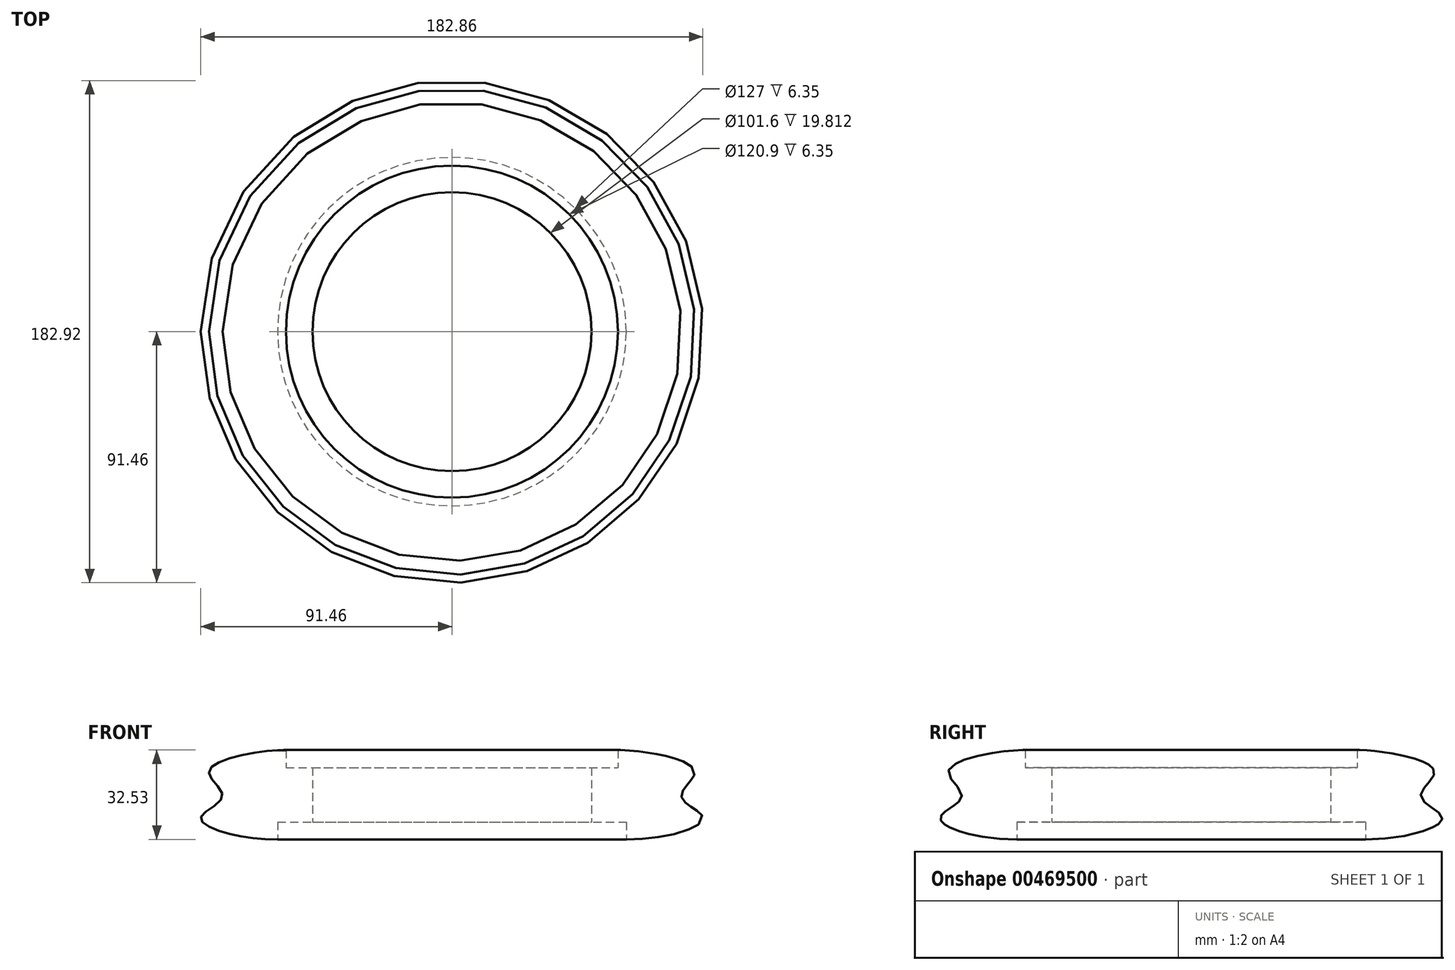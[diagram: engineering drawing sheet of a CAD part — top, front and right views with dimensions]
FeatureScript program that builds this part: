
annotation { "Feature Type Name" : "Feature", "Feature Type Description" : "" }
export const myFeature = defineFeature(function(context is Context, id is Id, definition is map)
    precondition{}
    {
        {
            var Q0;
            Q0=qCreatedBy(makeId("Front.planeOp"),FACE);
            var sketch = newSketch(context, id + "F0", { "sketchPlane" : qUnion([Q0])});
            skLineSegment(sketch, "E0", {"start": v(0, 0) * mm, "end": v(-63.5, 0) * mm, "construction": true});
            skLineSegment(sketch, "E1", {"start": v(0, 0) * mm, "end": v(0, 31.75) * mm, "construction": true});
            skLineSegment(sketch, "E2", {"start": v(-63.5, 0) * mm, "end": v(-63.5, 31.75) * mm, "construction": true});
            skLineSegment(sketch, "E3", {"start": v(-63.5, 31.75) * mm, "end": v(-69.85, 31.75) * mm, "construction": true});
            skLineSegment(sketch, "E4", {"start": v(-69.85, 31.75) * mm, "end": v(-69.85, 25.4) * mm, "construction": true});
            skLineSegment(sketch, "E5", {"start": v(-69.85, 25.4) * mm, "end": v(-69.85, 6.35) * mm, "construction": true});
            skLineSegment(sketch, "E6", {"start": v(-69.85, 6.35) * mm, "end": v(-69.85, 0) * mm, "construction": true});
            skSolve(sketch);
        }
        {
            var Q0;
            Q0=qCreatedBy(makeId("Front.planeOp"),FACE);
            var sketch = newSketch(context, id + "F1", { "sketchPlane" : qUnion([Q0])});
            skLineSegment(sketch, "E7", {"start": v(-60.45, 26.16) * mm, "end": v(-50.8, 26.16) * mm});
            skLineSegment(sketch, "E8", {"start": v(-60.45, 26.16) * mm, "end": v(-60.45, 32.51) * mm});
            skLineSegment(sketch, "E9", {"start": v(-63.5, 0) * mm, "end": v(-63.5, 6.35) * mm});
            skLineSegment(sketch, "E10", {"start": v(-63.5, 6.35) * mm, "end": v(-50.8, 6.35) * mm});
            skLineSegment(sketch, "E11", {"start": v(-50.8, 6.35) * mm, "end": v(-50.8, 26.16) * mm});
            skFitSpline(sketch, "E12", {"points": [v(-60.45, 32.51) * mm, v(-79.69, 29.9) * mm, v(-88.48, 23.87) * mm, v(-83.57, 15.59) * mm, v(-91.34, 8.31) * mm, v(-84.55, 3) * mm, v(-63.5, 0) * mm], "startDerivative": vector(-54.07, 2.17) * mm, "endDerivative": vector(103.66, 0) * mm});
            skSolve(sketch);
        }
        {
            var Q0;
            Q0=makeQuery(id+"F1.imprint","IMPRINT",FACE,{"disambiguationData":[TD([[makeQuery(id+"F1.imprint","IMPRINT",EDGE,{"derivedFrom":sQuery(id+"F1.wireOp",EDGE,"E7")}),-1.0]])]});
            var Q1;
            Q1=sQuery(id+"F0.wireOp",EDGE,"E1");
            revolve(context, id + "F2", {"entities" : qUnion([Q0]), "axis" : qUnion([Q1]), "revolveType" : RevolveType.FULL});
        }
    });
